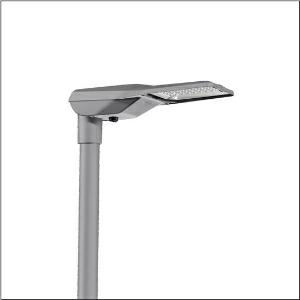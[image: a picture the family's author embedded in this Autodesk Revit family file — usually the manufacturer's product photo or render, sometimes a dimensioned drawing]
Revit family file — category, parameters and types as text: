
# Revit family: streetlight_sl_21_iq_mini___st1_0ab_5xe2m31u08gb_fb61
name_source: partatom
category: Lighting Fixtures
units: mm (PartAtom-declared; Revit-internal decimal feet)

## family parameters
Cut with Voids When Loaded = No
Host = Face
Light Source = No
Part Type = Normal
Room Calculation Point = No
Round Connector Dimension = Use Diameter
Shared = No

## types (1)
- --- (1 x LED, 5270 lm, 39.8 W, 3000K)
    Apparent Load = 40 VA
    CIE Flux Codes = 38 73 97 100 100
    Color Rendering = 70
    Color Temperature = 3000K
    Default Elevation = 1800 mm
    Description = Streetlight SL 21 iQ mini, mast luminaire, primary light control with lens, of PMMA, primary optical cover: cover, of toughened safety glass, transparent, light distribution: ST1.0aB, light emission: direct distribution, primary light characteristic: asymmetric, installation type: post-top, side-entry, LED, High Power LED, rated luminous flux: 5.270lm, luminous efficacy: 132lm/W, light colour: 730, colour temperature: 3000K, control: presetting dimming logarithmic, Street-Remote, Auto-Match, Temp-Guard, Lumen-Switch, Night-Set, Smart-Wire, Light-Fading, Desk-Remote (wireless, voltage-free reading and setting of iQ features in the workshop via application-optimized NFC function/RFID function), optimised constant luminous flux control (CLO 2.0), mains connection: 220..240V, AC, 50/60Hz, start of lifetime: 40W, end of service life: 41W, reduction: 18W, luminaire housing, of diecast aluminium, powder-coated, Siteco® metallic grey (DB 702S), corrosivity category C5 mid according to DIN EN ISO 12944, please order mast flange separately, inclination adjustable: 0°, 5°, 10°, 15°, sealing non-destructively replaceable, multi-level sealing system, length: 628mm, width: 235mm, height: 110mm, mast flange for spigot size: 42mm (side-entry): 5XC10008XM4, 60/48mm (side-entry/post-top): 5XC10108XM2, 76/60mm (side-entry/post-top): 5XC10108XM1, Smart Interface below, protection rating (complete): IP66, insulation class (complete): insulation class II (safety insulation), certification: CE, ENEC, ENEC+, VDE, impact resistance: IK09, permissible operating ambient temperature for outdoor applications: -40..+50°C, standard-compliant lighting for roads and squares, packaging unit: 1 piece

Light Distribution: ST1.0aB
    Height = 110 mm
    Lamp = 1 x LED
    Lamp Light Flux = 5270 lm
    Lamp Power = 39.8 W
    Lamp count = 1
    Length = 625 mm
    Luminous efficacy = 132 lm/W
    Manufacturer = Siteco
    ModVariant = No
    Model = 5XE2M31U08GB
    Number of Poles = 1
    OnlyDefault = Yes
    Power Factor = 1
    Product Name = Streetlight SL 21 iQ mini | ST1.0aB
    Product group = mast luminaire | pylon top
    ProductGroupID = 6100
    Protection Class = Protection class II
    Protection Degree = IP 66
    RLX_Detail_Level = 1
    RLX_Emergency_Light_Flux = 0 lm
    RLX_Emergency_Type = 0
    RLX_Emergency_Type_DB = No
    RlxData = <blob elided: 92601 chars, md5=62461150>
    Socket = socket
    Standby Power = 0 W
    System Light Flux = 5270 lm
    System Power = 40 W
    Type Comments = factory setting: luminous flux: 100 % | dim-lin: 254 | 800 mA
    Type Image = l_1003516.jpg
    URL = http://relux.com
    VarID = @adj_042677
    Voltage = 0 V
    Weight = 0.00 kg
    Width = 234 mm

## geometry (parser evidence)
native form markers: Blend x4, Sweep x11
no freeform markers — native parametric forms only
